# Revit family: HydroTap_Accessory_Zip_Font_Standalone
name_source: partatom
category: Plumbing Fixtures
revit_build: Autodesk Revit 2018 (Build: 20190510_1515(x64)
units: mm (PartAtom-declared; Revit-internal decimal feet)

## family parameters
Always vertical = Yes
Cut with Voids When Loaded = No
OmniClass Number = 23.45.55.11
OmniClass Title = Sanitary Components
Part Type = Normal
Room Calculation Point = No
Round Connector Dimension = Use Diameter
Shared = No
Work Plane-Based = Yes

## types (9) — shared parameters
CW Connection = No
Description = Standalone Font for Design Range Drinking Taps
HW Connection = No
IfcExportAs = IfcWasteTerminal
IfcExportType = NOTDEFINED
Manufacturer = Zip Australia
ManufacturerOverallDepth = 176 mm
ManufacturerOverallHeight = 52 mm
ManufacturerOverallWidth = 176 mm
ManufacturerURLProductSpecific = https://www.zipwater.com
ModifiedIssue = 20210406 $
URL = https://www.zipwater.com
Uniclass2015Code = Pr_40_70_23_42
Uniclass2015Title = Instant boiling and cold water taps
Uniclass2015Version = Products v1.17
Vent Connection = No
Waste Connection = Yes
zero-valued in all types: Default Elevation

## per-type parameters (varying)
| type | FixtureMaterial | ManufacturerSpecCode | Model | Type Comments |
| Matte White (Z14) | Metal_MatteWhite_Zip | 93441Z14 | Z14 | Matte White Finish |
| Brushed Stainless Steel (Z13) | Metal_BrushedStainlessSteel_Zip | 93441Z13 | Z13 | Brushed Stainless Steel Finish |
| Brushed Gold (Z07) | Metal_BrushedGold_Zip | 93441Z07 | Z07 | Brushed Gold Finish |
| Matte Black (Z03) | Metal_MatteBlack_Zip | 93441Z03 | Z03 | Matte Black Finish |
| Brushed Rose Gold (Z05) | Metal_BrushedRoseGold_Zip | 93441Z05 | Z05 | Brushed Rose Gold Finish |
| Chrome (Z00) | Metal_Chrome_Zip | 93441Z00 | Z00 | Chrome Finish |
| Gunmetal (Z09) | Metal_Gunmetal_Zip | 93441Z09 | Z09 | Gunmetal Finish |
| Brushed Nickel (Z11) | Metal_BrushedNickel_Zip | 93441Z11 | Z11 | Brushed Nickel Finish |
| Brushed Chrome (Z01) | Metal_BrushedChrome_Zip | 93441Z01 | Z01 | Brushed Chrome Finish |

## geometry (parser evidence)
native form markers: Sweep x3
no freeform markers — native parametric forms only
